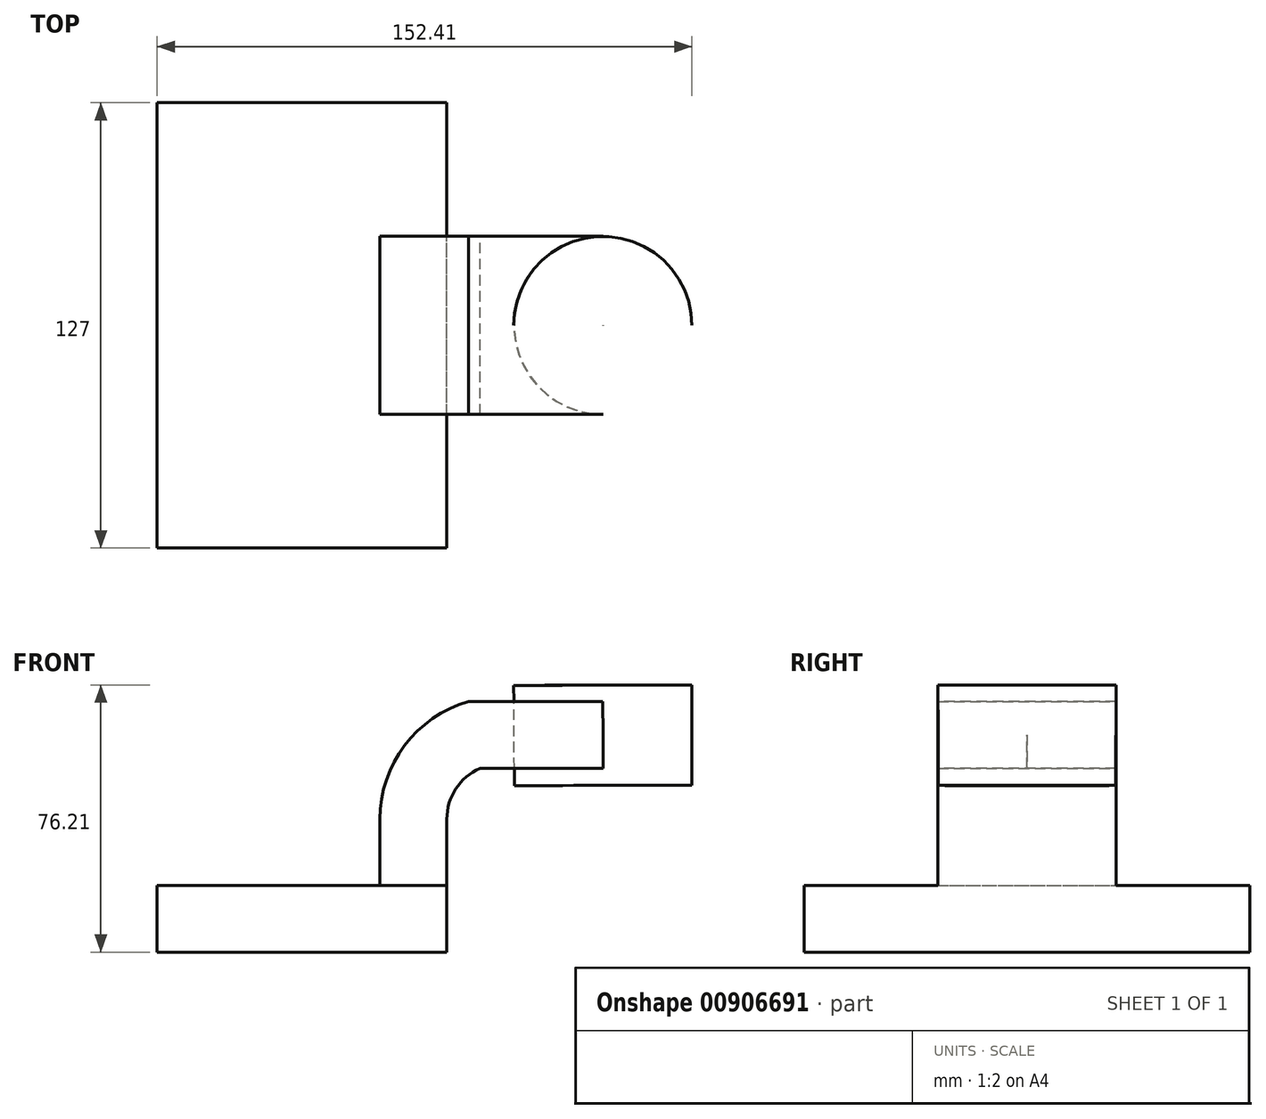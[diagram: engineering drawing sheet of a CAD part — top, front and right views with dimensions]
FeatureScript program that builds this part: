
annotation { "Feature Type Name" : "Feature", "Feature Type Description" : "" }
export const myFeature = defineFeature(function(context is Context, id is Id, definition is map)
    precondition{}
    {
        {
            var Q0;
            Q0=qCreatedBy(makeId("Front.planeOp"),FACE);
            var sketch = newSketch(context, id + "F0", { "sketchPlane" : qUnion([Q0])});
            skLineSegment(sketch, "E0.bottom", {"start": v(-41.28, 9.52) * mm, "end": v(41.27, 9.53) * mm});
            skLineSegment(sketch, "E0.top", {"start": v(-41.28, -9.53) * mm, "end": v(41.28, -9.53) * mm});
            skLineSegment(sketch, "E0.left", {"start": v(-41.28, 9.52) * mm, "end": v(-41.27, -9.53) * mm});
            skLineSegment(sketch, "E0.right", {"start": v(41.28, 9.53) * mm, "end": v(41.28, -9.52) * mm});
            skPoint(sketch, "E0.middle", {"position": v(0, 0) * mm});
            skLineSegment(sketch, "E1.bottom", {"start": v(60.32, 66.68) * mm, "end": v(111.12, 66.68) * mm});
            skLineSegment(sketch, "E1.top", {"start": v(60.33, 38.1) * mm, "end": v(111.12, 38.1) * mm});
            skLineSegment(sketch, "E1.left", {"start": v(60.32, 66.67) * mm, "end": v(60.32, 38.1) * mm});
            skLineSegment(sketch, "E1.right", {"start": v(111.12, 66.67) * mm, "end": v(111.12, 38.1) * mm});
            skPoint(sketch, "E1.middle", {"position": v(85.72, 52.39) * mm});
            skLineSegment(sketch, "E2", {"start": v(41.27, 9.53) * mm, "end": v(41.27, 28.36) * mm});
            skArc(sketch, "E3", {"start": v(41.27, 28.36) * mm, "mid": v(43.84, 37.02) * mm, "end": v(50.7, 42.88) * mm});
            skLineSegment(sketch, "E4", {"start": v(50.7, 42.88) * mm, "end": v(85.82, 42.88) * mm});
            skLineSegment(sketch, "E5.0", {"start": v(47.48, 61.93) * mm, "end": v(85.72, 61.93) * mm});
            skArc(sketch, "E5.1", {"start": v(22.22, 28.36) * mm, "mid": v(29.24, 49.36) * mm, "end": v(47.48, 61.93) * mm});
            skLineSegment(sketch, "E5.2", {"start": v(22.23, 9.53) * mm, "end": v(22.23, 28.36) * mm});
            skFitSpline(sketch, "E6", {"points": [v(-41.28, 9.53) * mm, v(47.48, 61.93) * mm], "startDerivative": vector(10.83, 93.3) * mm, "endDerivative": vector(118, 1.1) * mm});
            skLineSegment(sketch, "E7", {"start": v(85.72, 61.93) * mm, "end": v(85.82, 42.88) * mm});
            skPoint(sketch, "E8", {"position": v(85.72, 66.68) * mm});
            skLineSegment(sketch, "E9", {"start": v(85.72, 66.68) * mm, "end": v(85.82, 38.1) * mm});
            skSolve(sketch);
        }
        {
            var Q0;
            Q0=makeQuery(id+"F0.imprint","IMPRINT",FACE,{"disambiguationData":[TD([[makeQuery(id+"F0.imprint","IMPRINT",EDGE,{"derivedFrom":sQuery(id+"F0.wireOp",EDGE,"E0.top")}),1.0]])]});
            extrude(context, id + "F1", {"entities" : qUnion([Q0]), "endBound" : BoundingType.SYMMETRIC, "depth" : 127 * mm, "offsetDistance" : 25.4 * mm});
        }
        {
            var Q0;
            {var subQ1=sQuery(id+"F0.wireOp",EDGE,"E2");Q0=makeQuery(id+"F0.imprint","IMPRINT",FACE,{"disambiguationData":[TD([[makeQuery(id+"F0.imprint","IMPRINT",EDGE,{"derivedFrom":subQ1}),1.0]])]});}
            var Q1;
            {var subQ1=sQuery(id+"F0.wireOp",EDGE,"E5.0");var subQ5=sQuery(id+"F0.wireOp",EDGE,"E1.left");var subQ6=makeQuery(id+"F0.imprint","INTERSECT",VERTEX,{"derivedFrom":[subQ5,subQ1]});Q1=makeQuery(id+"F0.imprint","IMPRINT",FACE,{"disambiguationData":[TD([[makeQuery(id+"F0.imprint","IMPRINT",EDGE,{"disambiguationData":[TD([[subQ6,-1.0]])],"derivedFrom":subQ5}),1.0]])]});}
            extrude(context, id + "F2", {"entities" : qUnion([Q0, Q1]), "operationType" : NewBodyOperationType.ADD, "endBound" : BoundingType.SYMMETRIC, "depth" : 50.8 * mm, "offsetDistance" : 25.4 * mm});
        }
        {
            var Q0;
            Q0=makeQuery(id+"F0.imprint","IMPRINT",FACE,{"disambiguationData":[TD([[makeQuery(id+"F0.imprint","IMPRINT",EDGE,{"derivedFrom":sQuery(id+"F0.wireOp",EDGE,"E5.1")}),1.0]])]});
            extrude(context, id + "F3", {"entities" : qUnion([Q0]), "operationType" : NewBodyOperationType.ADD, "endBound" : BoundingType.SYMMETRIC, "depth" : 15.88 * mm, "offsetDistance" : 25.4 * mm});
        }
        {
            var Q0;
            {var subQ5=sQuery(id+"F0.wireOp",EDGE,"E1.right");Q0=makeQuery(id+"F0.imprint","IMPRINT",FACE,{"disambiguationData":[TD([[makeQuery(id+"F0.imprint","IMPRINT",EDGE,{"derivedFrom":subQ5}),-1.0]])]});}
            var Q1;
            Q1=sQuery(id+"F0.wireOp",EDGE,"E9");
            revolve(context, id + "F4", {"surfaceOperationType" : NewSurfaceOperationType.NEW, "entities" : qUnion([Q0]), "axis" : qUnion([Q1]), "revolveType" : RevolveType.FULL});
        }
    });
